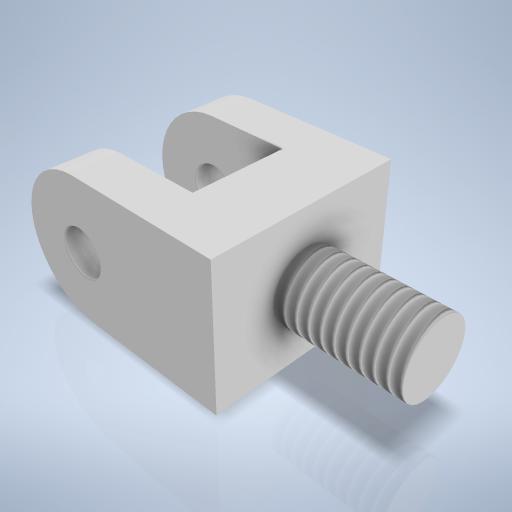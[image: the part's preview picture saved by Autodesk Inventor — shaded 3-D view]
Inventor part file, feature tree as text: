
AUTODESK INVENTOR PART (.ipt)
format: ipt  version: 2024.2 (Build 282272000, 272)  size: 289,792 bytes
history: native  units: mm
features: sketch x4, extrude x3, fillet x1, hole x1, thread x1
ambient origin geometry x8: Origin, YZ Plane, XZ Plane, XY Plane, X Axis, Y Axis, Z Axis, Center Point
bodies: Volumenkörper1 (feature_tree)
feature tree (10):
  extrude  "Extrusion1"  Depth=8.0mm
  fillet  "Rundung1"  Radius=8.0mm
  hole  "Bohrung2"  [1 undecoded]
  extrude  "Extrusion2"  Depth=2.0mm
  extrude  "Extrusion3"  Depth=3.0mm
  thread  "Gewinde1"  [1 undecoded]
  sketch  "Skizze1"  dims[d0=6.0mm d1=9.5mm d2=8.0mm d3=0.0mm]
  sketch  "Skizze3"  dims[d4=3.0mm d12=6.5mm]
  sketch  "Skizze4"  dims[d13=4.0mm d14=2.0mm]
  sketch  "Skizze5"  dims[d15=8.0mm d16=0.0mm d17=3.0mm d18=5.0mm d19=0.0mm d20=18.0mm d21=0.0mm d22=2.0mm d23=5.0mm d24=4.0mm d25=2.0mm d26=90.0deg d27=5.0mm d28=0.0mm]
note: 2 required parameter values undecoded (feature->parameter linkage not recoverable at this tier; creation-order binding heuristic only, values carry confidence <= 0.55)
